# Revit family: NaughtOne_HatchThreeSeatWork
name_source: partatom
category: Furniture
units: mm (PartAtom-declared; Revit-internal decimal feet)

## family parameters
Always vertical = Yes
Cut with Voids When Loaded = No
Enable Cutting in Views = No
Render Appearance Source = Family Geometry
Room Calculation Point = No
Shared = Yes
Work Plane-Based = No

## types (8) — shared parameters
Assembly Code = E2020200
AssetType = Moveable
BIMObjectName = Naughtone_Seating_Hatch
Category = Pr_40_50_12: Chairs, seats and benches
CodePerformance = PASSED BSEN 16139
Color = Various
DurationUnit = year
Export Type to IFC As = IfcFurnishingElementType
Finish = Upholstered
IfcExportAs = IfcFurnishingElementType
IfcExportType = SOFA
Is2Seat = Yes
Is3Seat = Yes
IsChair = No
Keynote = Pr_40_50_12
LeftOffset = 30.118 "
MainColor = Various
Manufacturer = naughtone
ManufacturerAddressUK = naughtone, Knaresborough Tech Park, Manse Lane, Knaresborough, HG5 8LF
ManufacturerName = Naughtone
ManufacturerURL = www.naughtone.com
Material = Fabric, leather/steel/solid wood/beech ply/foam
ModelNumber = HAT3RA
ModelReference = Hatch 3 Seater Right Arm
NBSDescription = Seating
NBSReference = 45-35-72/352
Name = Seating_Hatch_Naughtone
NominalHeight = 26.969 "
NominalWidth = 27.165 "
Package Qty = 1
Product Documentation Link = http://www.naughtone.com
ProductInformation = www.naughtone.com/portfolio-view/hatch
RightOffset = 30.118 "
Shape = Rectangular
Size = 1710x690x685mm
SustainabilityPerformance = FSC certified. FISP certified. ISO 14001 certified
Type IFC Predefined Type = SOFA
URL = http://www.hermanmiller.com
Uniclass2015Description = Chairs, seats and benches
Uniclass2015Reference = Pr_40_50_12
Uniclass2015Version = Products v1.5
Version = 1
VoidOffsetCentre = 10.039 "
WarrantyDurationLabor = 5
WarrantyDurationParts = 5
WarrantyDurationUnit = year
zero-valued in all types: Default Elevation, VoidOffset2Seat, VoidOffset3Seat

## per-type parameters (varying)
| type | Description | HasNoArms | HasOneArmL | HasOneArmR | HasTwoArms | Model |
| HAT3NA Single Work Ht | Hatch Three Seat No Arms Work height 18 inch seat height Single Fabric | Yes | No | No | No | NOHAN320W1 |
| HATNA Multiple Work Ht | Hatch Three Seat No Arms Work height 18 inch seat height Multiple Fabric | Yes | No | No | No | NOHAN320W2 |
| HAT3RA Single Work Ht | Hatch Three Seat Right Arm Work height 18 inch seat height Single Fabric | No | No | Yes | No | NOHAN330W1 |
| HAT3RA Multiple Work Ht | Hatch Three Seat Right Arm Work height 18 inch seat height Multiple Fabric | No | No | Yes | No | NOHAN330W2 |
| HAT3LA Single Work Ht | Hatch Three Seat Left Arm Work height 18 inch seat height Single Fabric | No | Yes | No | No | NOHAN340W1 |
| HAT3LA Multiple Work Ht | Hatch Three Seat Left Arm Work height 18 inch seat height Multiple Fabric | No | Yes | No | No | NOHAN340W2 |
| HAT32A Single Work Ht | Hatch Three Seat Two Arms Work height 18 inch seat height Single Fabric | No | No | No | Yes | NOHAN350W1 |
| HAT32A Multiple Work Ht | Hatch Three Seat Two Arms Work height 18 inch seat height Multiple Fabric | No | No | No | Yes | NOHAN350W2 |

## geometry (parser evidence)
native form markers: Sweep x4
no freeform markers — native parametric forms only
